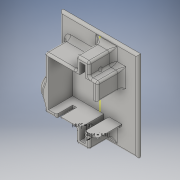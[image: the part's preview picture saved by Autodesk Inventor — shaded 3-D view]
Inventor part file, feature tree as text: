
AUTODESK INVENTOR PART (.ipt)
format: ipt  version: 2016 (Build 200138000, 138)  size: 634,368 bytes
history: native  units: in
note: dims shown in document units (in); Inventor stores cm internally (conversion verified against a paired STEP export)
features: fillet x10, sketch x9, extrude x6, hole x1
ambient origin geometry x8: Origin, YZ Plane, XZ Plane, XY Plane, X Axis, Y Axis, Z Axis, Center Point
bodies: Solid1 (feature_tree)
feature tree (26):
  extrude  "Extrusion1"  Depth=0.8976in
  fillet  "Fillet1"  Radius=0.1575in
  fillet  "Fillet2"  Radius=0.0394in
  extrude  "Extrusion4"  Depth=0.1004in
  extrude  "Extrusion5"  Depth=0.6142in
  hole  "Hole3"  [1 undecoded]
  fillet  "Fillet8"  Radius=0.1713in
  fillet  "Fillet9"  Radius=0.2992in
  extrude  "Extrusion6"  Depth=0.2165in
  sketch  "Sketch20"  dims[d92=0.2165in d93=0.2165in]
  sketch  "Sketch21"  dims[d95=0.9016in d97=0.0787in d98=0.0787in d99=0.0787in d100=0.0787in d101=0.0787in]
  extrude  "Extrusion7"  Depth=0.0787in
  fillet  "Fillet13"  Radius=0.0787in
  fillet  "Fillet14"  Radius=0.0787in
  fillet  "Fillet15"  Radius=0.0787in
  fillet  "Fillet16"  Radius=0.0787in
  extrude  "Extrusion8"  Depth=0.0394in
  fillet  "Fillet17"  Radius=0.0787in
  fillet  "Fillet18"  Radius=0.0394in
  sketch  "Sketch1"  dims[d2=0.1181in d3=0.0in d6=0.8976in d9=0.357in d10=0.7139in]
  sketch  "Sketch12"  dims[d11=0.0787in d12=0.0787in d13=0.0787in d14=0.0787in d45=0.1575in d46=0.0394in]
  sketch  "Sketch14"  dims[d82=0.9016in d83=0.8858in d85=0.1004in]
  sketch  "Sketch17"  dims[d86=0.1004in d87=0.6142in]
  sketch  "Sketch18"  dims[d88=0.6142in d89=0.1713in d90=0.1713in d91=0.2992in]
  sketch  "Sketch22"  dims[d102=0.0787in d103=0.1693in d105=0.0787in d106=0.0394in]
  sketch  "Sketch25"  dims[d107=0.0394in d108=0.0394in d109=0.0394in d110=0.1575in d111=0.0787in d112=0.0787in d113=0.0394in d114=0.9016in d125=0.0984in d130=0.185in d132=0.3543in d133=0.2165in d134=0.4724in d135=0.0in d136=0.0787in d137=0.315in d138=0.0in d139=0.0787in d144=0.0394in d145=0.7461in d146=0.0394in d147=0.07in d148=0.2362in d149=0.119in d150=0.0787in d151=0.5635in d152=0.315in d153=0.8108in d154=0.0787in d155=0.0394in d156=0.2717in d157=0.2323in d158=0.2756in d159=0.3937in d160=0.1575in d161=0.0in d164=0.2559in d165=0.0394in d166=0.1575in d167=0.0in d169=0.1535in d170=0.0787in d171=0.0787in d172=0.0394in d173=0.0906in d174=0.0in d175=0.0394in d176=0.0394in d26=0.0394in d27=0.0394in]
note: 1 required parameter value undecoded (feature->parameter linkage not recoverable at this tier; creation-order binding heuristic only, values carry confidence <= 0.55)
